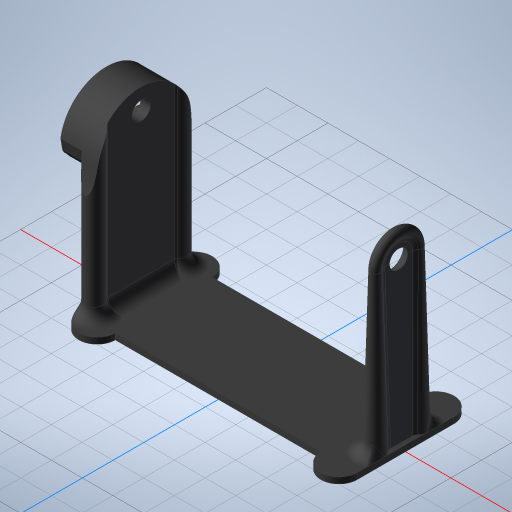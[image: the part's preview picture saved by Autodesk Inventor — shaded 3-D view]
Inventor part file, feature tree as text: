
AUTODESK INVENTOR PART (.ipt)
format: ipt  version: 2023 (Build 270158000, 158)  size: 1,140,736 bytes
history: native  units: in
note: dims shown in document units (in); Inventor stores cm internally (conversion verified against a paired STEP export)
features: extrude x27, sketch x20, projected_geometry x9, fillet x6, plane x3, revolve x2, split x2, other x2, sweep x1
ambient origin geometry x8: Origin, YZ Plane, XZ Plane, XY Plane, X Axis, Y Axis, Z Axis, Center Point
bodies: Solid1 (feature_tree), Solid2 (feature_tree)
feature tree (72):
  extrude  "Extrusion1"  Depth=3.1496in
  sketch  "Sketch2"  dims[d2=1.1811in d3=0.1969in d4=0.0in]
  extrude  "Extrusion2"  Depth=0.1969in TaperAngle=0.0deg
  extrude  "Extrusion3"  Depth=1.378in
  extrude  "Extrusion4"  Depth=0.5906in
  revolve  "Revolution1"  [1 undecoded]
  extrude  "Extrusion5"  Depth=1.1811in
  sketch  "Sketch4"  dims[d8=1.378in d9=0.5906in]
  extrude  "Extrusion7"  Depth=5.1181in
  extrude  "Extrusion8"  TaperAngle=0.0deg  [1 undecoded]
  extrude  "Extrusion9"  Depth=0.689in
  extrude  "Extrusion10"  TaperAngle=180.0deg  [1 undecoded]
  fillet  "Fillet2"  Radius=0.1067in
  sketch  "Sketch5"  dims[d10=0.5906in d11=0.1378in]
  extrude  "Extrusion11"  Depth=3.1496in TaperAngle=0.0deg
  extrude  "Extrusion12"  Depth=0.9055in
  extrude  "Extrusion13"  Depth=0.7874in TaperAngle=0.0deg
  sketch  "Sketch6"  dims[d12=1.5748in d13=1.1811in]
  extrude  "Extrusion14"  Depth=0.1181in TaperAngle=0.0deg
  revolve  "Revolution2"  [1 undecoded]
  extrude  "Extrusion6"  Depth=0.5512in
  extrude  "Extrusion15"  Depth=1.9882in
  extrude  "Extrusion16"  Depth=0.9646in
  sketch  "Sketch10"  dims[d18=0.689in d19=0.0in]
  sketch  "3D Sketch1"
  plane  "Work Plane1"
  sweep  "Sweep1"
  extrude  "Extrusion17"  Depth=0.6992in
  extrude  "Extrusion18"  TaperAngle=0.0deg  [1 undecoded]
  plane  "Work Plane2"
  split  "Split1"
  extrude  "Extrusion19"  Depth=2.1614in
  extrude  "Extrusion20"  Depth=0.1181in
  plane  "Work Plane3"
  extrude  "Extrusion21"  Depth=0.1181in
  fillet  "Fillet3"  Radius=0.1181in
  extrude  "Extrusion22"  Depth=0.1181in
  sketch  "Sketch16"  dims[d32=0.5906in d33=0.7874in d34=0.0in]
  extrude  "Extrusion24"  Depth=0.0787in
  extrude  "Extrusion25"  Depth=0.1969in TaperAngle=0.0deg
  sketch  "Sketch18"  dims[d39=0.1575in d40=0.0in d42=0.0394in]
  sketch  "Sketch19"  dims[d43=0.2756in d44=0.5512in]
  sketch  "Sketch20"  dims[d45=0.2953in d46=1.9882in]
  extrude  "Extrusion26"  Depth=0.0787in
  extrude  "Extrusion27"  Depth=0.1969in
  other  "Ruled Surface2"
  split  "Split2"
  extrude  "Extrusion28"  Depth=0.8189in TaperAngle=0.0deg
  fillet  "Fillet4"  Radius=0.1969in
  fillet  "Fillet5"  Radius=1.9685in
  fillet  "Fillet6"  Radius=1.9685in
  fillet  "Fillet7"  Radius=0.0787in
  sketch  "Sketch1"  dims[d0=9.0551in d1=3.1496in]
  sketch  "Sketch3"  dims[d5=0.315in d7=1.378in]
  projected_geometry  "Projected Loop1"
  sketch  "Sketch9"  dims[d14=5.9055in d15=0.0in d16=5.1181in d17=-0.0103in]
  projected_geometry  "Projected Loop6"
  projected_geometry  "Projected Loop7"
  projected_geometry  "Projected Loop8"
  projected_geometry  "Projected Loop9"
  sketch  "Sketch11"  dims[d20=0.689in d21=0.689in]
  sketch  "Sketch13"  dims[d22=5.1181in d23=-0.0069in d24=180.0deg d25=0.1067in]
  projected_geometry  "Projected Loop10"
  projected_geometry  "Projected Loop11"
  sketch  "Sketch14"  dims[d26=4.7244in d27=0.0in d28=3.1496in d29=0.0in]
  projected_geometry  "Projected Loop12"
  projected_geometry  "Projected Loop13"
  sketch  "Sketch15"  dims[d30=1.1811in d31=0.9055in]
  sketch  "Sketch17"  dims[d35=0.1181in d36=0.0in d37=0.1181in d38=0.0in]
  sketch  "Sketch21"  dims[d47=0.4724in d48=0.9646in]
  other  "Srf2"
  sketch  "Sketch22"  dims[d49=0.0in d50=2.252in d51=0.6992in d52=0.0in d53=2.1614in d54=0.1181in d55=0.1181in d56=0.1181in d57=0.1181in d61=0.0787in d62=0.1969in d63=0.0in d64=0.0787in d65=0.1969in d66=0.8189in d67=0.0in d68=0.1969in d69=0.0in d70=1.9685in d72=360.0deg d75=1.9685in d76=0.0787in d77=0.1969in d78=0.0in d79=180.0deg d80=0.5906in d81=0.0in d82=0.5906in d83=0.0in d84=0.0in d85=0.0in d86=0.3937in d87=0.0in d88=0.3937in d89=0.0in d90=3.1496in d91=0.0in d92=3.1496in d93=0.0in d95=0.2362in d96=0.2362in d97=0.3937in d98=0.0in d99=0.3937in d100=0.8189in d101=0.0in d104=0.1181in d105=0.1181in d106=0.1181in d107=0.1181in d108=0.8189in d109=0.0in d110=0.8189in d111=0.0in d112=0.1772in d113=0.1772in d114=0.1772in d115=0.1772in d116=0.1772in d117=0.1772in d118=0.1772in d119=0.1772in d120=0.248in d121=0.0in d122=0.248in d123=0.0in d130=3.1496in d131=0.0in d132=0.1772in d133=0.1772in d134=0.1772in d135=0.1772in d136=0.2362in d137=0.0in d138=0.3937in d139=0.1969in d140=0.0787in d141=0.0787in]
note: 5 required parameter values undecoded (feature->parameter linkage not recoverable at this tier; creation-order binding heuristic only, values carry confidence <= 0.55)